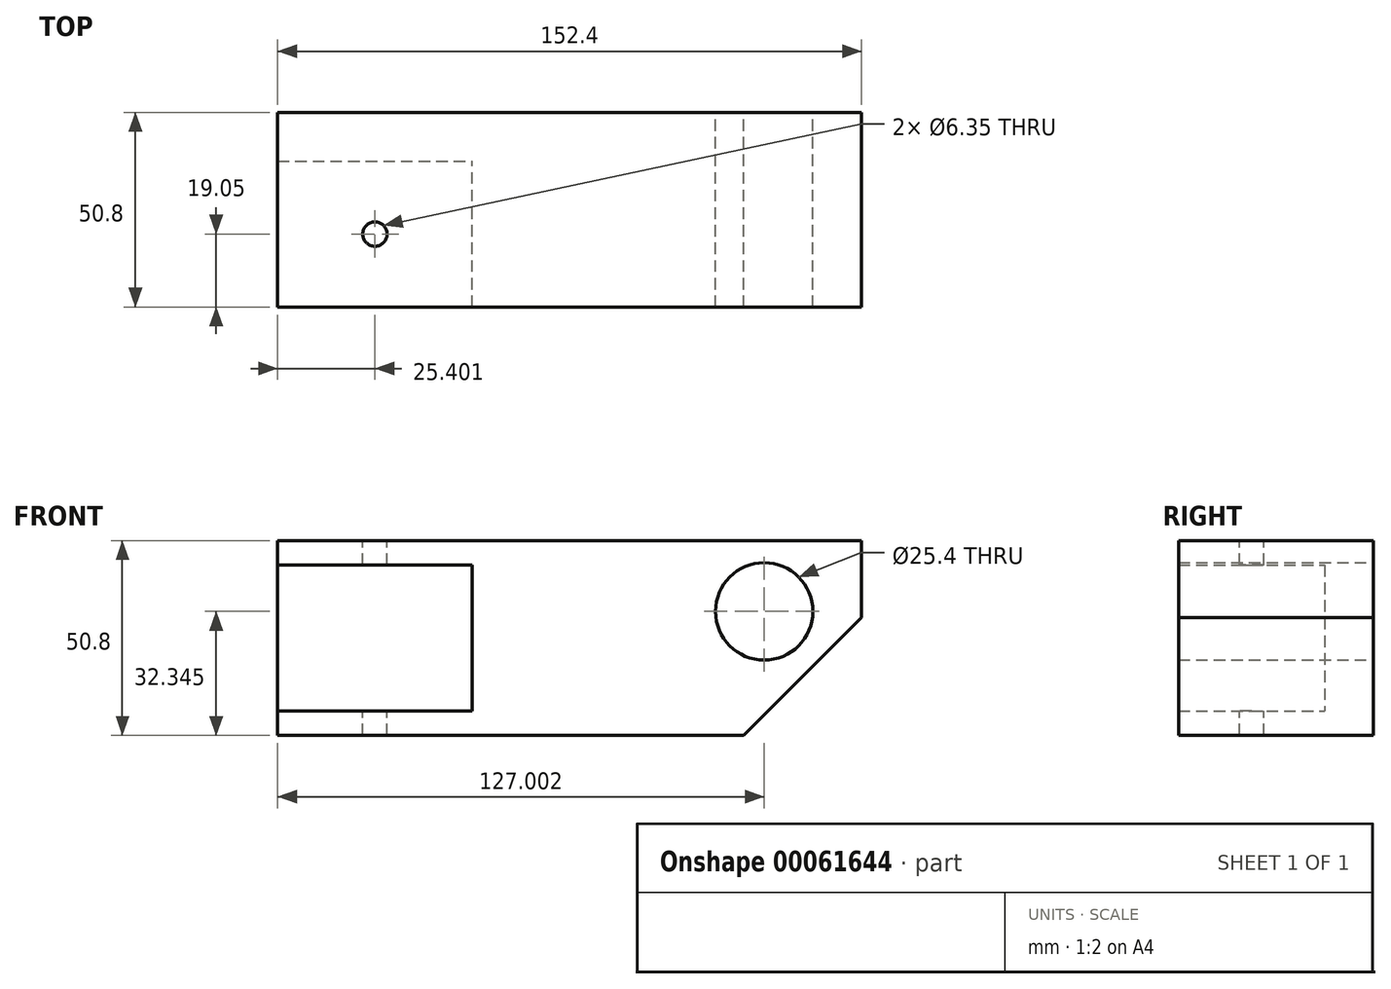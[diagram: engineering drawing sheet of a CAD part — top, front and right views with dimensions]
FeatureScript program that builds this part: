
annotation { "Feature Type Name" : "Feature", "Feature Type Description" : "" }
export const myFeature = defineFeature(function(context is Context, id is Id, definition is map)
    precondition{}
    {
        {
            var Q0;
            Q0=qCreatedBy(makeId("Front.planeOp"),FACE);
            var sketch = newSketch(context, id + "F0", { "sketchPlane" : qUnion([Q0])});
            skLineSegment(sketch, "E0", {"start": v(-140.8, 30.32) * mm, "end": v(-90, 30.32) * mm});
            skLineSegment(sketch, "E1", {"start": v(-90, 30.32) * mm, "end": v(-90, -7.78) * mm});
            skLineSegment(sketch, "E2", {"start": v(-90, -7.78) * mm, "end": v(-140.8, -7.78) * mm});
            skLineSegment(sketch, "E3", {"start": v(-140.8, -7.78) * mm, "end": v(-140.8, -14.13) * mm});
            skLineSegment(sketch, "E4", {"start": v(-140.8, -14.13) * mm, "end": v(-19.2, -14.13) * mm});
            skLineSegment(sketch, "E5", {"start": v(-19.2, -14.13) * mm, "end": v(11.6, 16.67) * mm});
            skLineSegment(sketch, "E6", {"start": v(11.6, 16.67) * mm, "end": v(11.6, 36.67) * mm});
            skLineSegment(sketch, "E7", {"start": v(11.6, 36.67) * mm, "end": v(-140.8, 36.67) * mm});
            skLineSegment(sketch, "E8", {"start": v(-140.8, 36.67) * mm, "end": v(-140.8, 30.32) * mm});
            skSolve(sketch);
        }
        {
            var Q0;
            Q0=makeQuery(id+"F0.imprint","IMPRINT",FACE,{"disambiguationData":[TD([[makeQuery(id+"F0.imprint","IMPRINT",EDGE,{"derivedFrom":sQuery(id+"F0.wireOp",EDGE,"E0")}),1.0]])]});
            extrude(context, id + "F1", {"entities" : qUnion([Q0]), "depth" : 50.8 * mm});
        }
        {
            var Q0;
            Q0=makeQuery(id+"F1.opExtrude","SWEPT_FACE",FACE,{"disambiguationData":[OSD([sQuery(id+"F0.wireOp",EDGE,"E1")])]});
            var sketch = newSketch(context, id + "F2", { "sketchPlane" : qUnion([Q0])});
            skLineSegment(sketch, "E9.bottom", {"start": v(0, 30.32) * mm, "end": v(12.7, 30.32) * mm});
            skLineSegment(sketch, "E9.top", {"start": v(0, -7.78) * mm, "end": v(12.7, -7.78) * mm});
            skLineSegment(sketch, "E9.left", {"start": v(0, 30.32) * mm, "end": v(0, -7.78) * mm});
            skLineSegment(sketch, "E9.right", {"start": v(12.7, 30.32) * mm, "end": v(12.7, -7.78) * mm});
            skSolve(sketch);
        }
        {
            var Q0;
            Q0=makeQuery(id+"F2.imprint","IMPRINT",FACE,{"disambiguationData":[TD([[makeQuery(id+"F2.imprint","IMPRINT",EDGE,{"derivedFrom":sQuery(id+"F2.wireOp",EDGE,"E9.bottom")}),1.0]])]});
            extrude(context, id + "F3", {"entities" : qUnion([Q0]), "operationType" : NewBodyOperationType.ADD, "depth" : 50.8 * mm});
        }
        {
            var Q0;
            Q0=makeQuery(id+"F1.opExtrude","CAP_FACE",FACE,{"disambiguationData":[OSD([sQuery(id+"F0.wireOp",EDGE,"E0"),sQuery(id+"F0.wireOp",EDGE,"E1"),sQuery(id+"F0.wireOp",EDGE,"E2"),sQuery(id+"F0.wireOp",EDGE,"E3"),sQuery(id+"F0.wireOp",EDGE,"E4"),sQuery(id+"F0.wireOp",EDGE,"E5"),sQuery(id+"F0.wireOp",EDGE,"E6"),sQuery(id+"F0.wireOp",EDGE,"E7"),sQuery(id+"F0.wireOp",EDGE,"E8")])],"isStart":true});
            var sketch = newSketch(context, id + "F4", { "sketchPlane" : qUnion([Q0])});
            skPoint(sketch, "E10", {"position": v(13.8, 18.22) * mm});
            skSolve(sketch);
        }
        {
            var Q0;
            Q0=sQuery(id+"F4.wireOp",VERTEX,"E10");
            var Q1;
            Q1=makeQuery(id+"F1.opExtrude","SWEPT_BODY",BODY,{"disambiguationData":[OSD([sQuery(id+"F0.wireOp",EDGE,"E0"),sQuery(id+"F0.wireOp",EDGE,"E1"),sQuery(id+"F0.wireOp",EDGE,"E2"),sQuery(id+"F0.wireOp",EDGE,"E3"),sQuery(id+"F0.wireOp",EDGE,"E4"),sQuery(id+"F0.wireOp",EDGE,"E5"),sQuery(id+"F0.wireOp",EDGE,"E6"),sQuery(id+"F0.wireOp",EDGE,"E7"),sQuery(id+"F0.wireOp",EDGE,"E8")])]});
            hole(context, id + "F5", {"style" : HoleStyle.SIMPLE, "holeDiameter" : 25.4 * mm, "endStyle" : HoleEndStyle.THROUGH, "locations" : qUnion([Q0]), "scope" : qUnion([Q1])});
        }
        {
            var Q0;
            Q0=makeQuery(id+"F1.opExtrude","SWEPT_FACE",FACE,{"disambiguationData":[OSD([sQuery(id+"F0.wireOp",EDGE,"E7")])]});
            var sketch = newSketch(context, id + "F6", { "sketchPlane" : qUnion([Q0])});
            skPoint(sketch, "E11", {"position": v(-115.4, -31.75) * mm});
            skSolve(sketch);
        }
        {
            var Q0;
            Q0=sQuery(id+"F6.wireOp",VERTEX,"a3bc4d88-bac8-46db-acfa-aece4eaeb009");
            var Q1;
            Q1=sQuery(id+"F6.wireOp",VERTEX,"E11");
            var Q2;
            Q2=makeQuery(id+"F1.opExtrude","SWEPT_BODY",BODY,{"disambiguationData":[OSD([sQuery(id+"F0.wireOp",EDGE,"E0"),sQuery(id+"F0.wireOp",EDGE,"E1"),sQuery(id+"F0.wireOp",EDGE,"E2"),sQuery(id+"F0.wireOp",EDGE,"E3"),sQuery(id+"F0.wireOp",EDGE,"E4"),sQuery(id+"F0.wireOp",EDGE,"E5"),sQuery(id+"F0.wireOp",EDGE,"E6"),sQuery(id+"F0.wireOp",EDGE,"E7"),sQuery(id+"F0.wireOp",EDGE,"E8")])]});
            hole(context, id + "F7", {"style" : HoleStyle.SIMPLE, "holeDiameter" : 6.35 * mm, "endStyle" : HoleEndStyle.THROUGH, "locations" : qUnion([Q0, Q1]), "scope" : qUnion([Q2])});
        }
    });
